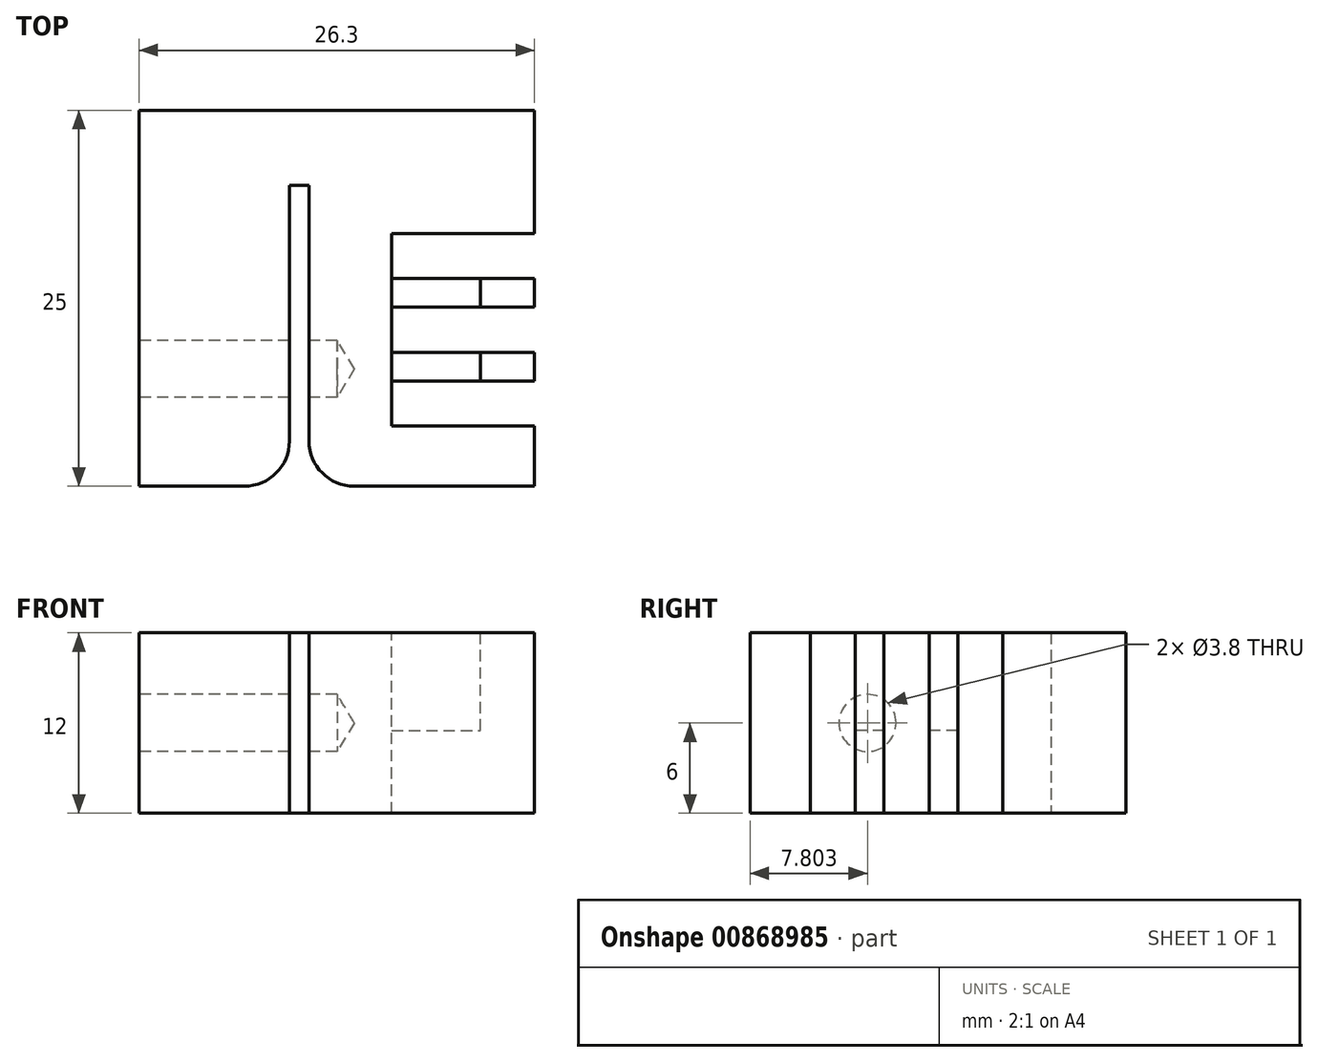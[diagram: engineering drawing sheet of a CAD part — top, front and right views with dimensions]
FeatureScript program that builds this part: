
annotation { "Feature Type Name" : "Feature", "Feature Type Description" : "" }
export const myFeature = defineFeature(function(context is Context, id is Id, definition is map)
    precondition{}
    {
        {
            var Q0;
            Q0=qCreatedBy(makeId("Top.planeOp"),FACE);
            var sketch = newSketch(context, id + "F0", { "sketchPlane" : qUnion([Q0])});
            skLineSegment(sketch, "E0.bottom", {"start": v(-11.3, 25) * mm, "end": v(15, 25) * mm});
            skLineSegment(sketch, "E0.top", {"start": v(-11.3, 0) * mm, "end": v(-1.3, 0) * mm});
            skLineSegment(sketch, "E0.left", {"start": v(-11.3, 25) * mm, "end": v(-11.3, 0) * mm});
            skLineSegment(sketch, "E0.right", {"start": v(15, 25) * mm, "end": v(15, 0) * mm});
            skLineSegment(sketch, "E1.top", {"start": v(-1.3, 20) * mm, "end": v(0, 20) * mm});
            skLineSegment(sketch, "E1.left", {"start": v(-1.3, 0) * mm, "end": v(-1.3, 20) * mm});
            skLineSegment(sketch, "E1.right", {"start": v(0, 0) * mm, "end": v(0, 20) * mm});
            skLineSegment(sketch, "E2.trimOffspring", {"start": v(0, 0) * mm, "end": v(15, 0) * mm});
            skLineSegment(sketch, "E3", {"start": v(0, 20) * mm, "end": v(0, 25) * mm});
            skSolve(sketch);
        }
        {
            var Q0;
            Q0=makeQuery(id+"F0.imprint","IMPRINT",FACE,{"disambiguationData":[TD([[makeQuery(id+"F0.imprint","IMPRINT",EDGE,{"derivedFrom":sQuery(id+"F0.wireOp",EDGE,"E0.top")}),1.0]])]});
            var Q1;
            {var subQ1=sQuery(id+"F0.wireOp",EDGE,"E0.right");Q1=makeQuery(id+"F0.imprint","IMPRINT",FACE,{"disambiguationData":[TD([[makeQuery(id+"F0.imprint","IMPRINT",EDGE,{"derivedFrom":subQ1}),-1.0]])]});}
            extrude(context, id + "F1", {"entities" : qUnion([Q0, Q1]), "depth" : 12 * mm});
        }
        {
            var Q0;
            Q0=makeQuery(id+"F1.opExtrude","CAP_FACE",FACE,{"disambiguationData":[OSD([sQuery(id+"F0.wireOp",EDGE,"E0.bottom"),sQuery(id+"F0.wireOp",EDGE,"E0.top"),sQuery(id+"F0.wireOp",EDGE,"E0.left"),sQuery(id+"F0.wireOp",EDGE,"E0.right"),sQuery(id+"F0.wireOp",EDGE,"E1.top"),sQuery(id+"F0.wireOp",EDGE,"E1.left"),sQuery(id+"F0.wireOp",EDGE,"E1.right"),sQuery(id+"F0.wireOp",EDGE,"E2.trimOffspring")])],"isStart":false});
            var sketch = newSketch(context, id + "F2", { "sketchPlane" : qUnion([Q0])});
            skLineSegment(sketch, "E4.bottom", {"start": v(5.5, 16.8) * mm, "end": v(11.4, 16.8) * mm});
            skLineSegment(sketch, "E4.top", {"start": v(5.5, 4) * mm, "end": v(11.4, 4) * mm});
            skLineSegment(sketch, "E4.left", {"start": v(5.5, 16.8) * mm, "end": v(5.5, 4) * mm});
            skLineSegment(sketch, "E4.right", {"start": v(11.4, 16.8) * mm, "end": v(11.4, 4) * mm});
            skLineSegment(sketch, "E5", {"start": v(11.4, 4) * mm, "end": v(15, 4) * mm});
            skSolve(sketch);
        }
        {
            var Q0;
            Q0=qSketchRegion(id+"F2",true);
            extrude(context, id + "F3", {"entities" : qUnion([Q0]), "operationType" : NewBodyOperationType.REMOVE, "oppositeDirection" : true, "depth" : 6.5 * mm});
        }
        {
            var Q0;
            Q0=makeQuery(id+"F1.opExtrude","CAP_FACE",FACE,{"disambiguationData":[OSD([sQuery(id+"F0.wireOp",EDGE,"E0.bottom"),sQuery(id+"F0.wireOp",EDGE,"E0.top"),sQuery(id+"F0.wireOp",EDGE,"E0.left"),sQuery(id+"F0.wireOp",EDGE,"E0.right"),sQuery(id+"F0.wireOp",EDGE,"E1.top"),sQuery(id+"F0.wireOp",EDGE,"E1.left"),sQuery(id+"F0.wireOp",EDGE,"E1.right"),sQuery(id+"F0.wireOp",EDGE,"E2.trimOffspring")])],"isStart":false});
            var sketch = newSketch(context, id + "F4", { "sketchPlane" : qUnion([Q0])});
            skLineSegment(sketch, "E6.bottom", {"start": v(5.5, 16.8) * mm, "end": v(15, 16.8) * mm});
            skLineSegment(sketch, "E6.top", {"start": v(5.5, 13.8) * mm, "end": v(15, 13.8) * mm});
            skLineSegment(sketch, "E6.left", {"start": v(5.5, 16.8) * mm, "end": v(5.5, 13.8) * mm});
            skLineSegment(sketch, "E6.right", {"start": v(15, 16.8) * mm, "end": v(15, 13.8) * mm});
            skLineSegment(sketch, "E7.bottom", {"start": v(5.5, 4) * mm, "end": v(15, 4) * mm});
            skLineSegment(sketch, "E7.top", {"start": v(5.5, 7) * mm, "end": v(15, 7) * mm});
            skLineSegment(sketch, "E7.left", {"start": v(5.5, 4) * mm, "end": v(5.5, 7) * mm});
            skLineSegment(sketch, "E7.right", {"start": v(15, 4) * mm, "end": v(15, 7) * mm});
            skLineSegment(sketch, "E8.bottom", {"start": v(5.5, 8.9) * mm, "end": v(15, 8.9) * mm});
            skLineSegment(sketch, "E8.top", {"start": v(5.5, 11.9) * mm, "end": v(15, 11.9) * mm});
            skLineSegment(sketch, "E8.left", {"start": v(5.5, 8.9) * mm, "end": v(5.5, 11.9) * mm});
            skLineSegment(sketch, "E8.right", {"start": v(15, 8.9) * mm, "end": v(15, 11.9) * mm});
            skLineSegment(sketch, "E9", {"start": v(5.5, 11.9) * mm, "end": v(5.5, 13.8) * mm});
            skLineSegment(sketch, "E10", {"start": v(5.5, 7) * mm, "end": v(5.5, 8.9) * mm});
            skSolve(sketch);
        }
        {
            var Q0;
            Q0=qSketchRegion(id+"F4",true);
            extrude(context, id + "F5", {"entities" : qUnion([Q0]), "operationType" : NewBodyOperationType.REMOVE, "endBound" : BoundingType.THROUGH_ALL, "oppositeDirection" : true, "depth" : 25 * mm});
        }
        {
            var Q0;
            Q0=makeQuery(id+"F1.opExtrude","SWEPT_EDGE",EDGE,{"disambiguationData":[OSD([sQuery(id+"F0.wireOp",EDGE,"E0.top"),sQuery(id+"F0.wireOp",EDGE,"E1.left")])]});
            var Q1;
            Q1=makeQuery(id+"F1.opExtrude","SWEPT_EDGE",EDGE,{"disambiguationData":[OSD([sQuery(id+"F0.wireOp",EDGE,"E1.right"),sQuery(id+"F0.wireOp",EDGE,"E2.trimOffspring")])]});
            fillet(context, id + "F6", {"entities" : qUnion([Q0, Q1]), "radius" : 3 * mm, "tangentPropagation" : true, "allowEdgeOverflow" : false});
        }
        {
            var Q0;
            Q0=makeQuery(id+"F1.opExtrude","SWEPT_FACE",FACE,{"disambiguationData":[OSD([sQuery(id+"F0.wireOp",EDGE,"E0.left")])]});
            var sketch = newSketch(context, id + "F7", { "sketchPlane" : qUnion([Q0])});
            skLineSegment(sketch, "E11", {"start": v(0, 6) * mm, "end": v(-27.92, 6) * mm, "construction": true});
            skLineSegment(sketch, "E12", {"start": v(-7.8, 17.58) * mm, "end": v(-7.8, -8.36) * mm, "construction": true});
            skPoint(sketch, "E13", {"position": v(-7.8, 6) * mm});
            skSolve(sketch);
        }
        {
            var Q0;
            Q0=sQuery(id+"F7.wireOp",VERTEX,"E13");
            var Q1;
            Q1=makeQuery(id+"F1.opExtrude","SWEPT_BODY",BODY,{"disambiguationData":[OSD([sQuery(id+"F0.wireOp",EDGE,"E0.bottom"),sQuery(id+"F0.wireOp",EDGE,"E0.top"),sQuery(id+"F0.wireOp",EDGE,"E0.left"),sQuery(id+"F0.wireOp",EDGE,"E0.right"),sQuery(id+"F0.wireOp",EDGE,"E1.top"),sQuery(id+"F0.wireOp",EDGE,"E1.left"),sQuery(id+"F0.wireOp",EDGE,"E1.right"),sQuery(id+"F0.wireOp",EDGE,"E2.trimOffspring")])]});
            hole(context, id + "F8", {"style" : HoleStyle.SIMPLE, "endStyle" : HoleEndStyle.BLIND, "standardTappedOrClearance" : lookupTablePath({ "standard" : "ANSI", "engagement" : "75%", "pitch" : "24 tpi", "size" : "#10", "type" : "Tapped" }), "standardBlindInLast" : lookupTablePath({ "standard" : "ANSI", "engagement" : "75%", "pitch" : "24 tpi", "size" : "#10", "type" : "Tapped" }), "holeDiameter" : 3.8 * mm, "majorDiameter" : 4.83 * mm, "showTappedDepth" : true, "holeDepth" : 13.18 * mm, "tappedDepth" : 10 * mm, "tapClearance" : 3, "locations" : qUnion([Q0]), "scope" : qUnion([Q1])});
        }
    });
